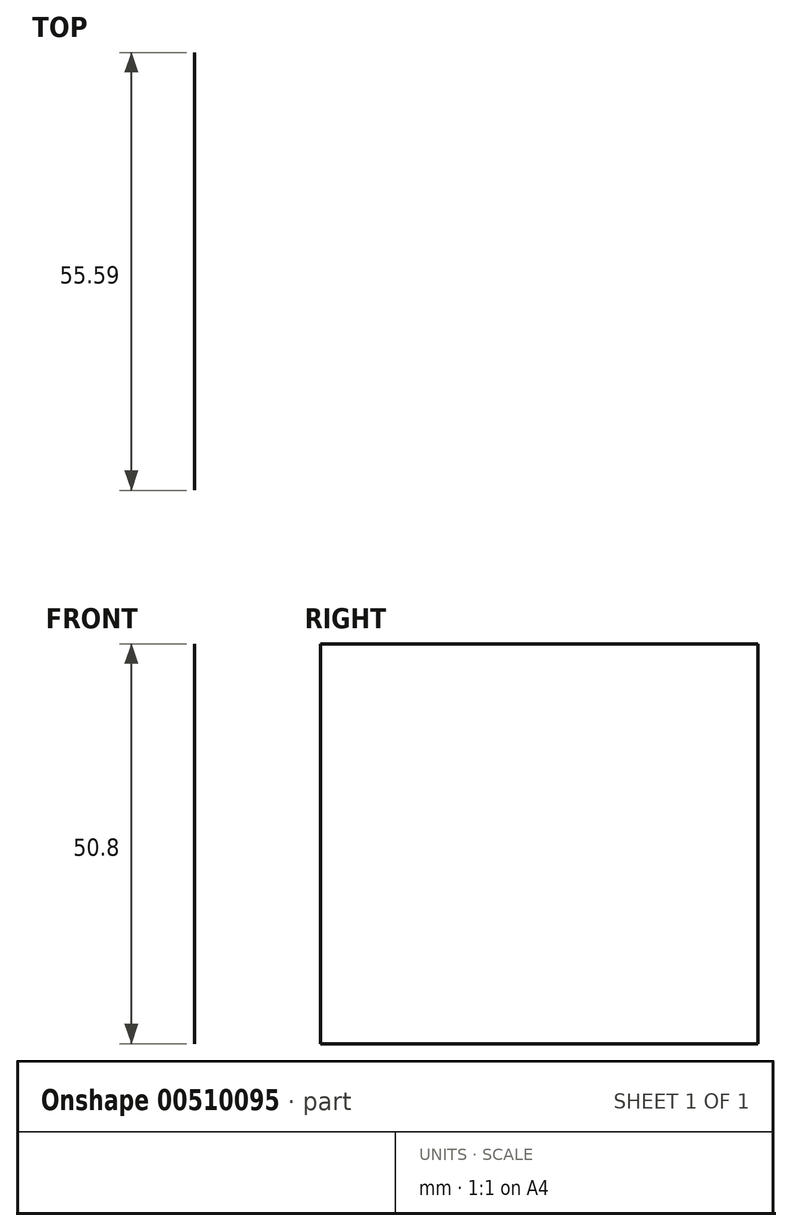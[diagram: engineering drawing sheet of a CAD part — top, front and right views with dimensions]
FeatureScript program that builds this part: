
annotation { "Feature Type Name" : "Feature", "Feature Type Description" : "" }
export const myFeature = defineFeature(function(context is Context, id is Id, definition is map)
    precondition{}
    {
        {
            var Q0;
            Q0=qCreatedBy(makeId("Top.planeOp"),FACE);
            var sketch = newSketch(context, id + "F0", { "sketchPlane" : qUnion([Q0])});
            skLineSegment(sketch, "E0.bottom", {"start": v(-27.24, 79.53) * mm, "end": v(0, 79.53) * mm});
            skLineSegment(sketch, "E0.top", {"start": v(-27.24, 46.02) * mm, "end": v(0, 46.02) * mm});
            skLineSegment(sketch, "E0.left", {"start": v(-27.24, 79.53) * mm, "end": v(-27.24, 46.02) * mm});
            skLineSegment(sketch, "E0.right", {"start": v(0, 79.53) * mm, "end": v(0, 46.02) * mm});
            skLineSegment(sketch, "E1.bottom", {"start": v(27.72, -34.3) * mm, "end": v(118.17, -34.3) * mm});
            skLineSegment(sketch, "E1.top", {"start": v(27.72, 21.28) * mm, "end": v(118.17, 21.28) * mm});
            skLineSegment(sketch, "E1.left", {"start": v(27.72, -34.3) * mm, "end": v(27.72, 21.28) * mm});
            skLineSegment(sketch, "E1.right", {"start": v(118.17, -34.3) * mm, "end": v(118.17, 21.28) * mm});
            skSolve(sketch);
        }
        {
            var Q0;
            Q0=sQuery(id+"F0.wireOp",EDGE,"E1.right");
            extrude(context, id + "F1", {"bodyType" : ToolBodyType.SURFACE, "surfaceEntities" : qUnion([Q0]), "depth" : 50.8 * mm});
        }
    });
